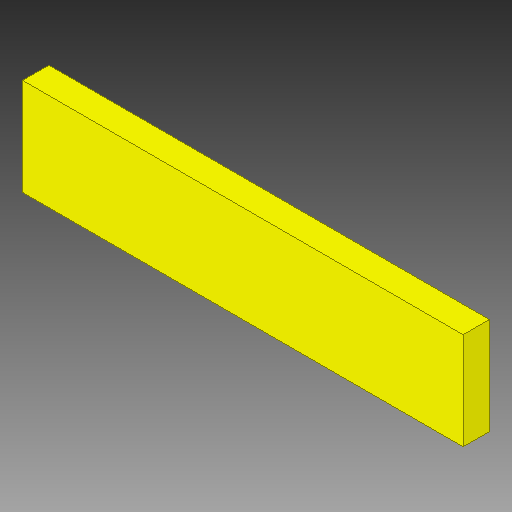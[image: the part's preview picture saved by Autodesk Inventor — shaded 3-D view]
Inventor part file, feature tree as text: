
AUTODESK INVENTOR PART (.ipt)
format: ipt  version: 2018 (Build 220112000, 112)  size: 80,896 bytes
history: native  units: in
note: dims shown in document units (in); Inventor stores cm internally (conversion verified against a paired STEP export)
features: other x1, extrude x1
ambient origin geometry x8: Origin, YZ Plane, XZ Plane, XY Plane, X Axis, Y Axis, Z Axis, Center Point
bodies: Solid1 (feature_tree)
feature tree (2):
  other  "LOGO16_TPLACE, U_1_LOGO16_TPLACE_154"
  extrude  "Extrusion1"  Depth=0.0394in TaperAngle=0.0deg
